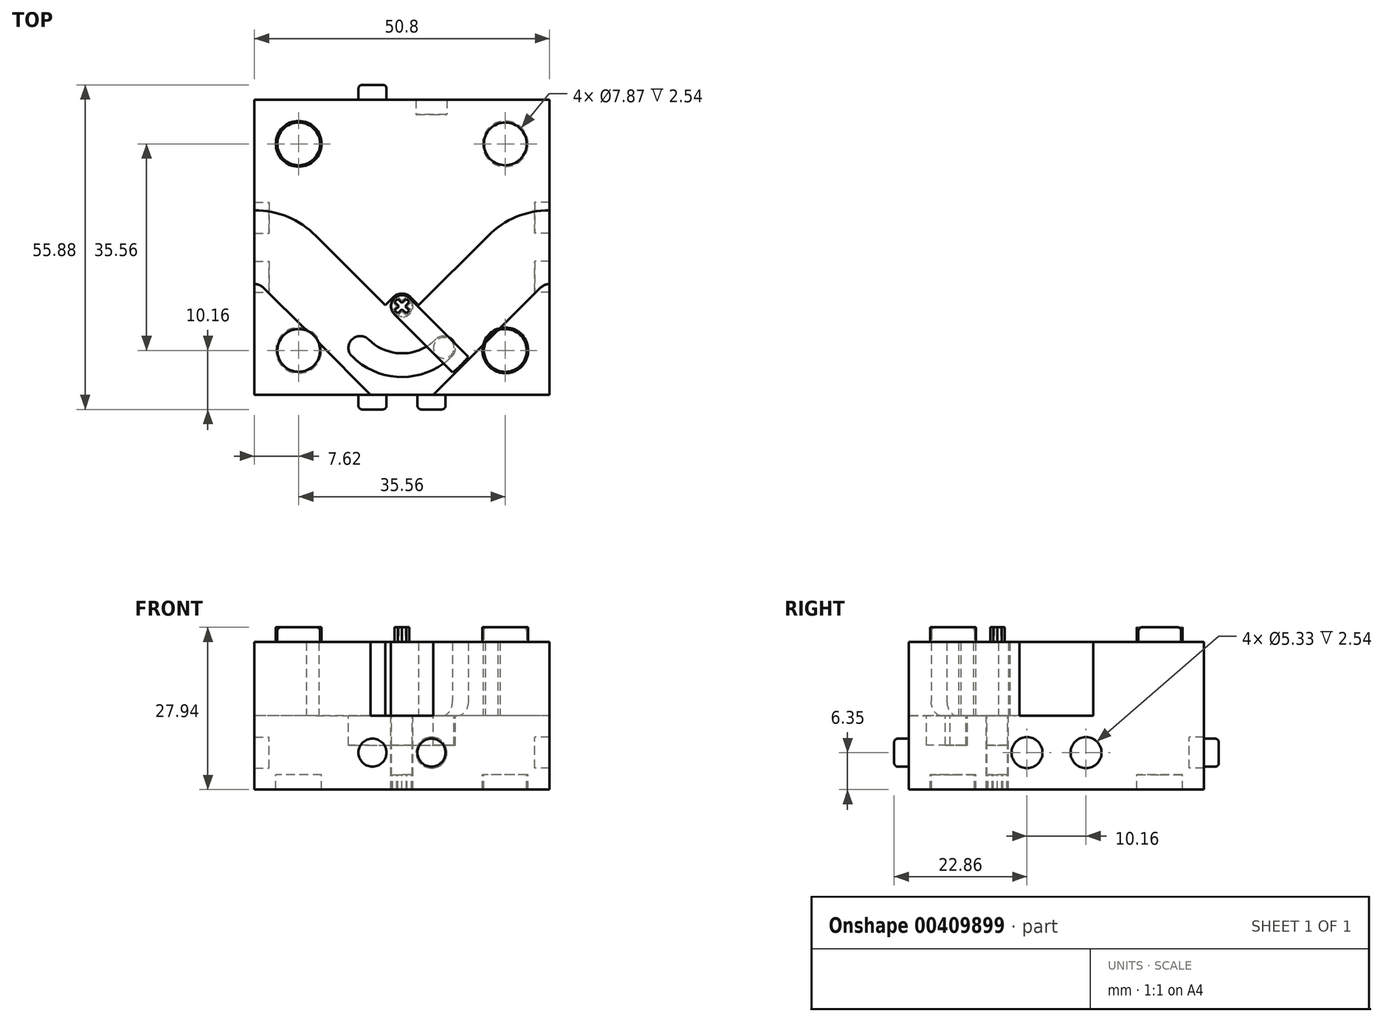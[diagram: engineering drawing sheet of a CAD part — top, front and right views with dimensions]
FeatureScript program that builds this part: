
annotation { "Feature Type Name" : "Feature", "Feature Type Description" : "" }
export const myFeature = defineFeature(function(context is Context, id is Id, definition is map)
    precondition{}
    {
        {
            var Q0;
            Q0=qCreatedBy(makeId("Top.planeOp"),FACE);
            var sketch = newSketch(context, id + "F0", { "sketchPlane" : qUnion([Q0])});
            skLineSegment(sketch, "E0.bottom", {"start": v(25.4, 25.4) * mm, "end": v(-25.4, 25.4) * mm});
            skLineSegment(sketch, "E0.top", {"start": v(25.4, -25.4) * mm, "end": v(-25.4, -25.4) * mm});
            skLineSegment(sketch, "E0.left", {"start": v(25.4, 25.4) * mm, "end": v(25.4, -25.4) * mm});
            skLineSegment(sketch, "E0.right", {"start": v(-25.4, 25.4) * mm, "end": v(-25.4, -25.4) * mm});
            skPoint(sketch, "E0.middle", {"position": v(0, 0) * mm});
            skPoint(sketch, "E1", {"position": v(25.4, 0) * mm});
            skPoint(sketch, "E2", {"position": v(-25.4, 0) * mm});
            skLineSegment(sketch, "E3", {"start": v(-25.4, 0) * mm, "end": v(25.4, 0) * mm, "construction": true});
            skLineSegment(sketch, "E4", {"start": v(0, 25.4) * mm, "end": v(0, -25.4) * mm, "construction": true});
            skCircle(sketch, "E5", {"center": v(0, 0) * mm, "radius": 2.54 * mm, "construction": true});
            skPoint(sketch, "E6", {"position": v(0, 2.54) * mm});
            skPoint(sketch, "E7", {"position": v(0, 5.08) * mm});
            skCircle(sketch, "E8", {"center": v(0, 0) * mm, "radius": 2.41 * mm});
            skCircle(sketch, "E9", {"center": v(0, 0) * mm, "radius": 2.67 * mm});
            skPoint(sketch, "E10", {"position": v(6.35, -25.4) * mm});
            skPoint(sketch, "E11", {"position": v(-6.35, -25.4) * mm});
            skCircle(sketch, "E12", {"center": v(0, 0) * mm, "radius": 5.08 * mm});
            skLineSegment(sketch, "E13", {"start": v(-6.35, -25.4) * mm, "end": v(6.35, -25.4) * mm});
            skLineSegment(sketch, "E14", {"start": v(-0.13, -26.91) * mm, "end": v(0.13, -26.91) * mm, "construction": true});
            skLineSegment(sketch, "E15", {"start": v(1.24, -2.36) * mm, "end": v(1.12, -2.14) * mm, "construction": true});
            skPoint(sketch, "E16", {"position": v(1.18, -2.25) * mm});
            skSolve(sketch);
        }
        {
            var Q0;
            Q0=qCreatedBy(makeId("Top.planeOp"),FACE);
            var sketch = newSketch(context, id + "F1", { "sketchPlane" : qUnion([Q0])});
            skLineSegment(sketch, "E17.0", {"start": v(1.35, -8.81) * mm, "end": v(11.4, -18.87) * mm});
            skLineSegment(sketch, "E18.0", {"start": v(8.71, -21.56) * mm, "end": v(-1.35, -11.5) * mm});
            skLineSegment(sketch, "E19.0", {"start": v(25.4, -25.4) * mm, "end": v(-25.4, -25.4) * mm});
            skLineSegment(sketch, "E20.0", {"start": v(25.4, 25.4) * mm, "end": v(25.4, 6.35) * mm});
            skLineSegment(sketch, "E21.0", {"start": v(25.4, 25.4) * mm, "end": v(-25.4, 25.4) * mm});
            skLineSegment(sketch, "E22.0", {"start": v(-25.4, 25.4) * mm, "end": v(-25.4, 6.35) * mm});
            skLineSegment(sketch, "E23", {"start": v(6.35, -38.04) * mm, "end": v(-6.35, -38.04) * mm, "construction": true});
            skLineSegment(sketch, "E24", {"start": v(35.56, -6.35) * mm, "end": v(35.56, 6.35) * mm, "construction": true});
            skPoint(sketch, "E25", {"position": v(0, -38.04) * mm});
            skPoint(sketch, "E26", {"position": v(35.56, 0) * mm});
            skLineSegment(sketch, "E27", {"start": v(10.15, -20.3) * mm, "end": v(0, -10.16) * mm, "construction": true});
            skLineSegment(sketch, "E28", {"start": v(14.82, 1.97) * mm, "end": v(2.87, -9.98) * mm});
            skLineSegment(sketch, "E29", {"start": v(0, -25.4) * mm, "end": v(0, 25.4) * mm, "construction": true});
            skLineSegment(sketch, "E30.trimOffspring", {"start": v(-25.4, -6.35) * mm, "end": v(-25.4, -25.4) * mm});
            skLineSegment(sketch, "E31.trimOffspring", {"start": v(25.4, -6.35) * mm, "end": v(25.4, -25.4) * mm});
            skArc(sketch, "E32", {"start": v(1.35, -8.81) * mm, "mid": v(-1.35, -8.81) * mm, "end": v(-1.35, -11.5) * mm});
            skArc(sketch, "E33", {"start": v(1.53, -8.63) * mm, "mid": v(0, -8) * mm, "end": v(-1.53, -8.63) * mm});
            skArc(sketch, "E34", {"start": v(25.4, 6.35) * mm, "mid": v(19.68, 5.21) * mm, "end": v(14.82, 1.97) * mm});
            skArc(sketch, "E35.MirrorCS", {"start": v(-25.4, 6.35) * mm, "mid": v(-19.68, 5.21) * mm, "end": v(-14.82, 1.97) * mm});
            skLineSegment(sketch, "E36.MirrorCS", {"start": v(-14.82, 1.97) * mm, "end": v(-2.87, -9.98) * mm});
            skLineSegment(sketch, "E37", {"start": v(-1.35, -11.5) * mm, "end": v(-2.87, -9.98) * mm, "construction": true});
            skLineSegment(sketch, "E38", {"start": v(-2.87, -9.98) * mm, "end": v(-2.87, -9.98) * mm});
            skLineSegment(sketch, "E39", {"start": v(-1.53, -8.63) * mm, "end": v(-2.87, -9.98) * mm});
            skLineSegment(sketch, "E40", {"start": v(1.53, -8.63) * mm, "end": v(2.87, -9.98) * mm});
            skLineSegment(sketch, "E41", {"start": v(-1.35, -11.5) * mm, "end": v(1.53, -8.63) * mm, "construction": true});
            skArc(sketch, "E42", {"start": v(-25.4, -6.35) * mm, "mid": v(-24.54, -6.52) * mm, "end": v(-23.8, -7.01) * mm});
            skLineSegment(sketch, "E43", {"start": v(-14.82, 1.97) * mm, "end": v(-25.4, -8.6) * mm, "construction": true});
            skLineSegment(sketch, "E44", {"start": v(-23.8, -7.01) * mm, "end": v(-11.85, -18.96) * mm});
            skLineSegment(sketch, "E45", {"start": v(-5.41, -25.4) * mm, "end": v(-10.33, -20.49) * mm});
            skLineSegment(sketch, "E46", {"start": v(-10.33, -20.49) * mm, "end": v(-10.33, -20.49) * mm});
            skLineSegment(sketch, "E47", {"start": v(-1.35, -11.5) * mm, "end": v(0, -10.16) * mm, "construction": true});
            skLineSegment(sketch, "E48", {"start": v(-10.33, -20.49) * mm, "end": v(-11.85, -18.96) * mm});
            skLineSegment(sketch, "E49.MirrorCS", {"start": v(5.41, -25.4) * mm, "end": v(10.33, -20.49) * mm});
            skLineSegment(sketch, "E50.MirrorCS", {"start": v(10.33, -20.49) * mm, "end": v(10.33, -20.49) * mm});
            skLineSegment(sketch, "E51.MirrorCS", {"start": v(10.33, -20.49) * mm, "end": v(11.85, -18.96) * mm});
            skLineSegment(sketch, "E52.MirrorCS", {"start": v(23.8, -7.01) * mm, "end": v(11.85, -18.96) * mm});
            skArc(sketch, "E53", {"start": v(25.4, -6.35) * mm, "mid": v(24.54, -6.52) * mm, "end": v(23.8, -7.01) * mm});
            skPoint(sketch, "E54", {"position": v(0, 0) * mm});
            skLineSegment(sketch, "E55", {"start": v(-0.98, -8.53) * mm, "end": v(-1.11, -8.31) * mm, "construction": true});
            skLineSegment(sketch, "E56", {"start": v(10.33, -20.49) * mm, "end": v(10.15, -20.3) * mm, "construction": true});
            skCircle(sketch, "E57", {"center": v(0, -10.16) * mm, "radius": 14.35 * mm});
            skSolve(sketch);
        }
        {
            var Q0;
            Q0=qCreatedBy(makeId("Top.planeOp"),FACE);
            var sketch = newSketch(context, id + "F2", { "sketchPlane" : qUnion([Q0])});
            skLineSegment(sketch, "E58.0", {"start": v(-25.4, 25.4) * mm, "end": v(-25.4, -25.4) * mm, "construction": true});
            skLineSegment(sketch, "E58.1", {"start": v(0, 25.4) * mm, "end": v(0, -25.4) * mm, "construction": true});
            skLineSegment(sketch, "E58.2", {"start": v(-25.4, 0) * mm, "end": v(25.4, 0) * mm, "construction": true});
            skLineSegment(sketch, "E58.3", {"start": v(25.4, 25.4) * mm, "end": v(-25.4, 25.4) * mm, "construction": true});
            skLineSegment(sketch, "E58.4", {"start": v(25.4, -25.4) * mm, "end": v(-25.4, -25.4) * mm, "construction": true});
            skLineSegment(sketch, "E58.5", {"start": v(25.4, 25.4) * mm, "end": v(25.4, -25.4) * mm, "construction": true});
            skCircle(sketch, "E59", {"center": v(17.78, 17.78) * mm, "radius": 3.81 * mm, "construction": true});
            skLineSegment(sketch, "E60", {"start": v(17.78, 17.78) * mm, "end": v(17.78, 25.4) * mm, "construction": true});
            skLineSegment(sketch, "E61", {"start": v(17.78, 17.78) * mm, "end": v(25.4, 17.78) * mm, "construction": true});
            skLineSegment(sketch, "E62", {"start": v(19.27, 14.41) * mm, "end": v(19.38, 14.18) * mm, "construction": true});
            skCircle(sketch, "E63", {"center": v(17.78, 17.78) * mm, "radius": 3.68 * mm});
            skCircle(sketch, "E64", {"center": v(17.78, 17.78) * mm, "radius": 3.94 * mm});
            skCircle(sketch, "E65.MirrorC", {"center": v(17.78, -17.78) * mm, "radius": 3.94 * mm});
            skCircle(sketch, "E66.MirrorC", {"center": v(17.78, -17.78) * mm, "radius": 3.68 * mm});
            skCircle(sketch, "E67.MirrorC", {"center": v(-17.78, -17.78) * mm, "radius": 3.68 * mm});
            skCircle(sketch, "E68.MirrorC", {"center": v(-17.78, -17.78) * mm, "radius": 3.94 * mm});
            skCircle(sketch, "E69.MirrorC", {"center": v(-17.78, 17.78) * mm, "radius": 3.68 * mm});
            skCircle(sketch, "E70.MirrorC", {"center": v(-17.78, 17.78) * mm, "radius": 3.94 * mm});
            skPoint(sketch, "E71.positionSnap0", {"position": v(19.33, 14.3) * mm});
            skLineSegment(sketch, "E72.0", {"start": v(1.17, -9) * mm, "end": v(-1.17, -11.33) * mm, "construction": true});
            skLineSegment(sketch, "E73.0", {"start": v(1.17, -11.33) * mm, "end": v(-1.17, -9) * mm, "construction": true});
            skLineSegment(sketch, "E74", {"start": v(1.08, -11.24) * mm, "end": v(0.72, -11.6) * mm, "construction": true});
            skLineSegment(sketch, "E75", {"start": v(0.72, -11.6) * mm, "end": v(0, -10.88) * mm, "construction": true});
            skLineSegment(sketch, "E76", {"start": v(0, -10.16) * mm, "end": v(0, -11.06) * mm, "construction": true});
            skLineSegment(sketch, "E77", {"start": v(0.99, -11.15) * mm, "end": v(0.72, -11.42) * mm});
            skLineSegment(sketch, "E78", {"start": v(0.72, -11.42) * mm, "end": v(0, -10.7) * mm});
            skLineSegment(sketch, "E79", {"start": v(1.17, -11.33) * mm, "end": v(0.72, -11.78) * mm});
            skLineSegment(sketch, "E80", {"start": v(0.72, -11.78) * mm, "end": v(0, -11.06) * mm});
            skLineSegment(sketch, "E81", {"start": v(0.96, -11.18) * mm, "end": v(1.14, -11.36) * mm, "construction": true});
            skLineSegment(sketch, "E82", {"start": v(0.63, -11.33) * mm, "end": v(0.45, -11.5) * mm, "construction": true});
            skLineSegment(sketch, "E83.MirrorCS", {"start": v(1.62, -10.88) * mm, "end": v(0.9, -10.16) * mm});
            skLineSegment(sketch, "E84.MirrorCS", {"start": v(0.99, -11.15) * mm, "end": v(1.26, -10.88) * mm});
            skLineSegment(sketch, "E85.MirrorCS", {"start": v(1.17, -11.33) * mm, "end": v(1.62, -10.88) * mm});
            skLineSegment(sketch, "E86.MirrorCS", {"start": v(1.26, -10.88) * mm, "end": v(0.54, -10.16) * mm});
            skLineSegment(sketch, "E87.MirrorCS", {"start": v(-0.99, -11.15) * mm, "end": v(-0.72, -11.42) * mm});
            skLineSegment(sketch, "E88.MirrorCS", {"start": v(-1.62, -10.88) * mm, "end": v(-0.9, -10.16) * mm});
            skLineSegment(sketch, "E89.MirrorCS", {"start": v(-0.72, -11.42) * mm, "end": v(0, -10.7) * mm});
            skLineSegment(sketch, "E90.MirrorCS", {"start": v(-0.99, -11.15) * mm, "end": v(-1.26, -10.88) * mm});
            skLineSegment(sketch, "E91.MirrorCS", {"start": v(-1.17, -11.33) * mm, "end": v(-0.72, -11.78) * mm});
            skLineSegment(sketch, "E92.MirrorCS", {"start": v(-1.17, -11.33) * mm, "end": v(-1.62, -10.88) * mm});
            skLineSegment(sketch, "E93.MirrorCS", {"start": v(-1.26, -10.88) * mm, "end": v(-0.54, -10.16) * mm});
            skLineSegment(sketch, "E94.MirrorCS", {"start": v(-0.72, -11.78) * mm, "end": v(0, -11.06) * mm});
            skLineSegment(sketch, "E95", {"start": v(0, -10.16) * mm, "end": v(0.9, -10.16) * mm, "construction": true});
            skLineSegment(sketch, "E96.MirrorCS", {"start": v(1.62, -9.44) * mm, "end": v(0.9, -10.16) * mm});
            skLineSegment(sketch, "E97.MirrorCS", {"start": v(1.26, -9.44) * mm, "end": v(0.54, -10.16) * mm});
            skLineSegment(sketch, "E98.MirrorCS", {"start": v(1.17, -9) * mm, "end": v(1.62, -9.44) * mm});
            skLineSegment(sketch, "E99.MirrorCS", {"start": v(0.99, -9.17) * mm, "end": v(1.26, -9.44) * mm});
            skLineSegment(sketch, "E100.MirrorCS", {"start": v(0.99, -9.17) * mm, "end": v(0.72, -8.9) * mm});
            skLineSegment(sketch, "E101.MirrorCS", {"start": v(1.17, -9) * mm, "end": v(0.72, -8.54) * mm});
            skLineSegment(sketch, "E102.MirrorCS", {"start": v(0.72, -8.9) * mm, "end": v(0, -9.62) * mm});
            skLineSegment(sketch, "E103.MirrorCS", {"start": v(0.72, -8.54) * mm, "end": v(0, -9.26) * mm});
            skLineSegment(sketch, "E104.MirrorCS", {"start": v(-0.72, -8.9) * mm, "end": v(0, -9.62) * mm});
            skLineSegment(sketch, "E105.MirrorCS", {"start": v(-0.72, -8.54) * mm, "end": v(0, -9.26) * mm});
            skLineSegment(sketch, "E106.MirrorCS", {"start": v(-0.99, -9.17) * mm, "end": v(-0.72, -8.9) * mm});
            skLineSegment(sketch, "E107.MirrorCS", {"start": v(-1.17, -9) * mm, "end": v(-0.72, -8.54) * mm});
            skLineSegment(sketch, "E108.MirrorCS", {"start": v(-0.99, -9.17) * mm, "end": v(-1.26, -9.44) * mm});
            skLineSegment(sketch, "E109.MirrorCS", {"start": v(-1.26, -9.44) * mm, "end": v(-0.54, -10.16) * mm});
            skLineSegment(sketch, "E110.MirrorCS", {"start": v(-1.62, -9.44) * mm, "end": v(-0.9, -10.16) * mm});
            skLineSegment(sketch, "E111.MirrorCS", {"start": v(-1.17, -9) * mm, "end": v(-1.62, -9.44) * mm});
            skPoint(sketch, "E112.0", {"position": v(0, -10.16) * mm});
            skSolve(sketch);
        }
        {
            var Q0;
            Q0=qCreatedBy(makeId("Top.planeOp"),FACE);
            var sketch = newSketch(context, id + "F3", { "sketchPlane" : qUnion([Q0])});
            skLineSegment(sketch, "E113.0", {"start": v(25.4, -25.4) * mm, "end": v(-25.4, -25.4) * mm});
            skLineSegment(sketch, "E114.0", {"start": v(25.4, 25.4) * mm, "end": v(25.4, -25.4) * mm});
            skLineSegment(sketch, "E115.0", {"start": v(25.4, 25.4) * mm, "end": v(-25.4, 25.4) * mm});
            skLineSegment(sketch, "E116.0", {"start": v(-25.4, 25.4) * mm, "end": v(-25.4, -25.4) * mm});
            skPoint(sketch, "E117.0", {"position": v(0, -10.16) * mm});
            skLineSegment(sketch, "E118.0", {"start": v(8.98, -19.14) * mm, "end": v(0, -10.16) * mm, "construction": true});
            skCircle(sketch, "E119", {"center": v(7.18, -17.34) * mm, "radius": 1.9 * mm, "construction": true});
            skLineSegment(sketch, "E120", {"start": v(8.51, -18.53) * mm, "end": v(8.7, -18.7) * mm, "construction": true});
            skPoint(sketch, "E121", {"position": v(8.6, -18.61) * mm});
            skArc(sketch, "E122", {"start": v(8.62, -18.78) * mm, "mid": v(8.62, -15.9) * mm, "end": v(5.75, -15.9) * mm});
            skCircle(sketch, "E123", {"center": v(7.18, -17.34) * mm, "radius": 1.78 * mm});
            skLineSegment(sketch, "E124", {"start": v(0, -25.4) * mm, "end": v(0, -10.16) * mm, "construction": true});
            skArc(sketch, "E125.MirrorCS", {"start": v(-8.62, -18.78) * mm, "mid": v(-8.62, -15.9) * mm, "end": v(-5.75, -15.9) * mm});
            skArc(sketch, "E126", {"start": v(8.62, -18.78) * mm, "mid": v(0, -22.35) * mm, "end": v(-8.62, -18.78) * mm});
            skArc(sketch, "E127", {"start": v(5.75, -15.9) * mm, "mid": v(0, -18.29) * mm, "end": v(-5.75, -15.9) * mm});
            skLineSegment(sketch, "E128", {"start": v(7.18, -17.34) * mm, "end": v(7.37, -19.11) * mm, "construction": true});
            skLineSegment(sketch, "E129", {"start": v(7.18, -17.34) * mm, "end": v(6.12, -15.76) * mm, "construction": true});
            skCircle(sketch, "E130", {"center": v(0, -10.16) * mm, "radius": 1.78 * mm});
            skCircle(sketch, "E131", {"center": v(0, -10.16) * mm, "radius": 1.9 * mm});
            skLineSegment(sketch, "E132", {"start": v(0, -10.16) * mm, "end": v(0.96, -11.65) * mm, "construction": true});
            skLineSegment(sketch, "E133", {"start": v(0, -10.16) * mm, "end": v(1.04, -11.76) * mm, "construction": true});
            skSolve(sketch);
        }
        {
            var Q0;
            Q0=qCreatedBy(makeId("Top.planeOp"),FACE);
            var sketch = newSketch(context, id + "F4", { "sketchPlane" : qUnion([Q0])});
            skCircle(sketch, "E134.0", {"center": v(0, -10.16) * mm, "radius": 1.78 * mm});
            skCircle(sketch, "E134.1", {"center": v(0, -10.16) * mm, "radius": 1.9 * mm});
            skLineSegment(sketch, "E135.0", {"start": v(25.4, 25.4) * mm, "end": v(25.4, -25.4) * mm});
            skLineSegment(sketch, "E136.0", {"start": v(25.4, 25.4) * mm, "end": v(-25.4, 25.4) * mm});
            skLineSegment(sketch, "E137.0", {"start": v(-25.4, 25.4) * mm, "end": v(-25.4, -25.4) * mm});
            skLineSegment(sketch, "E138.0", {"start": v(25.4, -25.4) * mm, "end": v(-25.4, -25.4) * mm});
            skSolve(sketch);
        }
        {
            var Q0;
            {var subQ0=sQuery(id+"F1.wireOp",EDGE,"E31.trimOffspring");Q0=makeQuery(id+"F1.imprint","IMPRINT",FACE,{"disambiguationData":[TD([[makeQuery(id+"F1.imprint","IMPRINT",EDGE,{"derivedFrom":subQ0}),-1.0]])]});}
            var Q1;
            Q1=makeQuery(id+"F1.imprint","IMPRINT",FACE,{"disambiguationData":[TD([[makeQuery(id+"F1.imprint","IMPRINT",EDGE,{"derivedFrom":sQuery(id+"F1.wireOp",EDGE,"E20.0")}),-1.0]])]});
            var Q2;
            {var subQ0=sQuery(id+"F1.wireOp",EDGE,"E30.trimOffspring");Q2=makeQuery(id+"F1.imprint","IMPRINT",FACE,{"disambiguationData":[TD([[makeQuery(id+"F1.imprint","IMPRINT",EDGE,{"derivedFrom":subQ0}),1.0]])]});}
            var Q3;
            Q3=makeQuery(id+"F1.imprint","IMPRINT",FACE,{"disambiguationData":[TD([[makeQuery(id+"F1.imprint","IMPRINT",EDGE,{"derivedFrom":sQuery(id+"F1.wireOp",EDGE,"E33")}),-1.0]])]});
            var Q4;
            {var subQ0=sQuery(id+"F1.wireOp",EDGE,"E17.0");Q4=makeQuery(id+"F1.imprint","IMPRINT",FACE,{"disambiguationData":[TD([[makeQuery(id+"F1.imprint","IMPRINT",EDGE,{"derivedFrom":subQ0}),-1.0]])]});}
            var Q5;
            {var subQ0=sQuery(id+"F1.wireOp",EDGE,"E28");Q5=makeQuery(id+"F1.imprint","IMPRINT",FACE,{"disambiguationData":[TD([[makeQuery(id+"F1.imprint","IMPRINT",EDGE,{"derivedFrom":subQ0}),-1.0]])]});}
            extrude(context, id + "F5", {"entities" : qUnion([Q0, Q1, Q2, Q3, Q4, Q5]), "depth" : 12.7 * mm});
        }
        {
            var Q0;
            Q0=makeQuery(id+"F2.imprint","IMPRINT",FACE,{"disambiguationData":[TD([[makeQuery(id+"F2.imprint","IMPRINT",EDGE,{"derivedFrom":sQuery(id+"F2.wireOp",EDGE,"E66.MirrorC")}),-1.0]])]});
            var Q1;
            Q1=makeQuery(id+"F2.imprint","IMPRINT",FACE,{"disambiguationData":[TD([[makeQuery(id+"F2.imprint","IMPRINT",EDGE,{"derivedFrom":sQuery(id+"F2.wireOp",EDGE,"E63")}),1.0]])]});
            var Q2;
            Q2=makeQuery(id+"F2.imprint","IMPRINT",FACE,{"disambiguationData":[TD([[makeQuery(id+"F2.imprint","IMPRINT",EDGE,{"derivedFrom":sQuery(id+"F2.wireOp",EDGE,"E69.MirrorC")}),-1.0]])]});
            var Q3;
            Q3=makeQuery(id+"F2.imprint","IMPRINT",FACE,{"disambiguationData":[TD([[makeQuery(id+"F2.imprint","IMPRINT",EDGE,{"derivedFrom":sQuery(id+"F2.wireOp",EDGE,"E67.MirrorC")}),1.0]])]});
            var Q4;
            {var subQ1=sQuery(id+"F2.wireOp",EDGE,"E77");Q4=makeQuery(id+"F2.imprint","IMPRINT",FACE,{"disambiguationData":[TD([[makeQuery(id+"F2.imprint","IMPRINT",EDGE,{"derivedFrom":subQ1}),-1.0]])]});}
            extrude(context, id + "F6", {"entities" : qUnion([Q0, Q1, Q2, Q3, Q4]), "operationType" : NewBodyOperationType.ADD, "depth" : 15.24 * mm});
        }
        {
            var Q0;
            Q0=makeQuery(id+"F3.imprint","IMPRINT",FACE,{"disambiguationData":[TD([[makeQuery(id+"F3.imprint","IMPRINT",EDGE,{"derivedFrom":sQuery(id+"F3.wireOp",EDGE,"E113.0")}),-1.0]])]});
            var Q1;
            Q1=makeQuery(id+"F3.imprint","IMPRINT",FACE,{"disambiguationData":[TD([[makeQuery(id+"F3.imprint","IMPRINT",EDGE,{"derivedFrom":sQuery(id+"F3.wireOp",EDGE,"E123")}),1.0]])]});
            var Q2;
            Q2=makeQuery(id+"F3.imprint","IMPRINT",FACE,{"disambiguationData":[TD([[makeQuery(id+"F3.imprint","IMPRINT",EDGE,{"derivedFrom":sQuery(id+"F3.wireOp",EDGE,"E130")}),1.0]])]});
            extrude(context, id + "F7", {"entities" : qUnion([Q0, Q1, Q2]), "oppositeDirection" : true, "depth" : 5.08 * mm});
        }
        {
            var Q0;
            Q0=makeQuery(id+"F4.imprint","IMPRINT",FACE,{"disambiguationData":[TD([[makeQuery(id+"F4.imprint","IMPRINT",EDGE,{"derivedFrom":sQuery(id+"F4.wireOp",EDGE,"E134.1")}),-1.0]])]});
            var Q1;
            Q1=makeQuery(id+"F4.imprint","IMPRINT",FACE,{"disambiguationData":[TD([[makeQuery(id+"F4.imprint","IMPRINT",EDGE,{"derivedFrom":sQuery(id+"F4.wireOp",EDGE,"E134.0")}),1.0]])]});
            extrude(context, id + "F8", {"entities" : qUnion([Q0, Q1]), "oppositeDirection" : true, "depth" : 12.7 * mm, "hasSecondDirection" : true, "secondDirectionOppositeDirection" : true, "secondDirectionDepth" : 5.08 * mm});
        }
        {
            var Q0;
            Q0=makeQuery(id+"F2.imprint","IMPRINT",FACE,{"disambiguationData":[TD([[makeQuery(id+"F2.imprint","IMPRINT",EDGE,{"derivedFrom":sQuery(id+"F2.wireOp",EDGE,"E67.MirrorC")}),1.0]])]});
            var Q1;
            Q1=makeQuery(id+"F2.imprint","IMPRINT",FACE,{"disambiguationData":[TD([[makeQuery(id+"F2.imprint","IMPRINT",EDGE,{"derivedFrom":sQuery(id+"F2.wireOp",EDGE,"E67.MirrorC")}),-1.0]])]});
            var Q2;
            Q2=makeQuery(id+"F2.imprint","IMPRINT",FACE,{"disambiguationData":[TD([[makeQuery(id+"F2.imprint","IMPRINT",EDGE,{"derivedFrom":sQuery(id+"F2.wireOp",EDGE,"E69.MirrorC")}),-1.0]])]});
            var Q3;
            Q3=makeQuery(id+"F2.imprint","IMPRINT",FACE,{"disambiguationData":[TD([[makeQuery(id+"F2.imprint","IMPRINT",EDGE,{"derivedFrom":sQuery(id+"F2.wireOp",EDGE,"E69.MirrorC")}),1.0]])]});
            var Q4;
            Q4=makeQuery(id+"F2.imprint","IMPRINT",FACE,{"disambiguationData":[TD([[makeQuery(id+"F2.imprint","IMPRINT",EDGE,{"derivedFrom":sQuery(id+"F2.wireOp",EDGE,"E63")}),1.0]])]});
            var Q5;
            Q5=makeQuery(id+"F2.imprint","IMPRINT",FACE,{"disambiguationData":[TD([[makeQuery(id+"F2.imprint","IMPRINT",EDGE,{"derivedFrom":sQuery(id+"F2.wireOp",EDGE,"E63")}),-1.0]])]});
            var Q6;
            Q6=makeQuery(id+"F2.imprint","IMPRINT",FACE,{"disambiguationData":[TD([[makeQuery(id+"F2.imprint","IMPRINT",EDGE,{"derivedFrom":sQuery(id+"F2.wireOp",EDGE,"E66.MirrorC")}),-1.0]])]});
            var Q7;
            Q7=makeQuery(id+"F2.imprint","IMPRINT",FACE,{"disambiguationData":[TD([[makeQuery(id+"F2.imprint","IMPRINT",EDGE,{"derivedFrom":sQuery(id+"F2.wireOp",EDGE,"E65.MirrorC")}),-1.0]])]});
            var Q8;
            {var subQ3=sQuery(id+"F2.wireOp",EDGE,"E78");Q8=makeQuery(id+"F2.imprint","IMPRINT",FACE,{"disambiguationData":[TD([[makeQuery(id+"F2.imprint","IMPRINT",EDGE,{"derivedFrom":subQ3}),-1.0]])]});}
            var Q9;
            {var subQ6=sQuery(id+"F2.wireOp",EDGE,"E78");Q9=makeQuery(id+"F2.imprint","IMPRINT",FACE,{"disambiguationData":[TD([[makeQuery(id+"F2.imprint","IMPRINT",EDGE,{"derivedFrom":subQ6}),1.0]])]});}
            var Q10;
            {var subQ3=sQuery(id+"F2.wireOp",EDGE,"E81");Q10=makeQuery(id+"F2.imprint","IMPRINT",FACE,{"disambiguationData":[TD([[makeQuery(id+"F2.imprint","IMPRINT",EDGE,{"derivedFrom":subQ3}),1.0]])]});}
            extrude(context, id + "F9", {"entities" : qUnion([Q0, Q1, Q2, Q3, Q4, Q5, Q6, Q7, Q8, Q9, Q10]), "operationType" : NewBodyOperationType.REMOVE, "oppositeDirection" : true, "depth" : 12.7 * mm, "hasSecondDirection" : true, "secondDirectionOppositeDirection" : true, "secondDirectionDepth" : 10.16 * mm});
        }
        {
            var Q0;
            Q0=makeQuery(id+"F5.opExtrude","SWEPT_BODY",BODY,{"disambiguationData":[OSD([sQuery(id+"F1.wireOp",EDGE,"07ce15e0-389a-4b33-b96a-b9eb0d6417ea.0"),sQuery(id+"F1.wireOp",EDGE,"2ea3173f-9e5d-47db-bc64-ed2cd4916a22.0"),sQuery(id+"F1.wireOp",EDGE,"1fc487c8-3388-41be-b45a-3c84602bca13.0"),sQuery(id+"F1.wireOp",EDGE,"E19.0"),sQuery(id+"F1.wireOp",EDGE,"E31.trimOffspring")])]});
            var Q1;
            Q1=makeQuery(id+"F7.opExtrude","SWEPT_BODY",BODY,{"disambiguationData":[OSD([sQuery(id+"F3.wireOp",EDGE,"E113.0"),sQuery(id+"F3.wireOp",EDGE,"E114.0"),sQuery(id+"F3.wireOp",EDGE,"E115.0"),sQuery(id+"F3.wireOp",EDGE,"E116.0"),sQuery(id+"F3.wireOp",EDGE,"E122"),sQuery(id+"F3.wireOp",EDGE,"E125.MirrorCS"),sQuery(id+"F3.wireOp",EDGE,"E126"),sQuery(id+"F3.wireOp",EDGE,"E127"),sQuery(id+"F3.wireOp",EDGE,"E131")])]});
            var Q2;
            Q2=makeQuery(id+"F5.opExtrude","SWEPT_BODY",BODY,{"disambiguationData":[OSD([sQuery(id+"F1.wireOp",EDGE,"90c61b00-249b-4847-8f0a-689f453f4bd6.0"),sQuery(id+"F1.wireOp",EDGE,"aaa51523-57ab-4ff3-b2ff-3d760ec803aa.0"),sQuery(id+"F1.wireOp",EDGE,"1fc487c8-3388-41be-b45a-3c84602bca13.0"),sQuery(id+"F1.wireOp",EDGE,"E19.0"),sQuery(id+"F1.wireOp",EDGE,"E30.trimOffspring")])]});
            var Q3;
            Q3=makeQuery(id+"F8.opExtrude","SWEPT_BODY",BODY,{"disambiguationData":[OSD([sQuery(id+"F4.wireOp",EDGE,"E134.1"),sQuery(id+"F4.wireOp",EDGE,"E135.0"),sQuery(id+"F4.wireOp",EDGE,"E136.0"),sQuery(id+"F4.wireOp",EDGE,"E137.0"),sQuery(id+"F4.wireOp",EDGE,"E138.0")])]});
            var Q4;
            Q4=makeQuery(id+"F5.opExtrude","SWEPT_BODY",BODY,{"disambiguationData":[OSD([sQuery(id+"F1.wireOp",EDGE,"d973afc5-03ed-41d9-9e6c-79cc070b5d1a.0"),sQuery(id+"F1.wireOp",EDGE,"1fc487c8-3388-41be-b45a-3c84602bca13.0"),sQuery(id+"F1.wireOp",EDGE,"E20.0"),sQuery(id+"F1.wireOp",EDGE,"E21.0"),sQuery(id+"F1.wireOp",EDGE,"E22.0"),sQuery(id+"F1.wireOp",EDGE,"b72e6335-8749-4926-bdcc-0623d4d98a26")])]});
            booleanBodies(context, id + "F10", {"operationType" : BooleanOperationType.UNION, "tools" : qUnion([Q0, Q1, Q2, Q3, Q4])});
        }
        {
            var Q0;
            Q0=qCreatedBy(makeId("Right.planeOp"),FACE);
            var sketch = newSketch(context, id + "F11", { "sketchPlane" : qUnion([Q0])});
            skPoint(sketch, "E139", {"position": v(-5.08, -6.35) * mm});
            skPoint(sketch, "E140", {"position": v(-2.67, -6.35) * mm});
            skPoint(sketch, "E141", {"position": v(-2.41, -6.35) * mm});
            skPoint(sketch, "E142", {"position": v(2.41, -6.35) * mm});
            skPoint(sketch, "E143", {"position": v(2.67, -6.35) * mm});
            skPoint(sketch, "E144", {"position": v(5.08, -6.35) * mm});
            skCircle(sketch, "E145", {"center": v(-5.08, -6.35) * mm, "radius": 2.41 * mm});
            skCircle(sketch, "E146", {"center": v(-5.08, -6.35) * mm, "radius": 2.67 * mm});
            skCircle(sketch, "E147", {"center": v(5.08, -6.35) * mm, "radius": 2.41 * mm});
            skCircle(sketch, "E148", {"center": v(5.08, -6.35) * mm, "radius": 2.67 * mm});
            skLineSegment(sketch, "E149", {"start": v(-2.67, 0) * mm, "end": v(-5.08, 0) * mm});
            skLineSegment(sketch, "E150", {"start": v(5.08, 0) * mm, "end": v(2.67, 0) * mm});
            skLineSegment(sketch, "E151", {"start": v(-2.41, 0) * mm, "end": v(-2.67, 0) * mm});
            skLineSegment(sketch, "E152", {"start": v(2.67, 0) * mm, "end": v(2.41, 0) * mm});
            skLineSegment(sketch, "E153", {"start": v(-25.4, 0) * mm, "end": v(-25.4, -12.7) * mm});
            skLineSegment(sketch, "E154", {"start": v(25.4, -12.7) * mm, "end": v(25.4, 12.7) * mm});
            skPoint(sketch, "E155", {"position": v(-25.4, -6.35) * mm});
            skPoint(sketch, "E156", {"position": v(25.4, 0) * mm});
            skPoint(sketch, "E157", {"position": v(25.4, -6.35) * mm});
            skSolve(sketch);
        }
        {
            var Q0;
            Q0=qCreatedBy(makeId("Front.planeOp"),FACE);
            var sketch = newSketch(context, id + "F12", { "sketchPlane" : qUnion([Q0])});
            skPoint(sketch, "E158", {"position": v(-154.37, 0) * mm});
            skPoint(sketch, "E159", {"position": v(-154.37, -6.35) * mm});
            skPoint(sketch, "E160", {"position": v(5.08, -6.35) * mm});
            skPoint(sketch, "E161", {"position": v(2.67, -6.35) * mm});
            skPoint(sketch, "E162", {"position": v(2.41, -6.35) * mm});
            skPoint(sketch, "E163", {"position": v(-2.41, -6.35) * mm});
            skPoint(sketch, "E164", {"position": v(-2.67, -6.35) * mm});
            skPoint(sketch, "E165", {"position": v(-5.08, -6.35) * mm});
            skCircle(sketch, "E166", {"center": v(5.08, -6.35) * mm, "radius": 2.41 * mm});
            skCircle(sketch, "E167", {"center": v(5.08, -6.35) * mm, "radius": 2.67 * mm});
            skCircle(sketch, "E168", {"center": v(-5.08, -6.35) * mm, "radius": 2.67 * mm});
            skCircle(sketch, "E169", {"center": v(-5.08, -6.35) * mm, "radius": 2.41 * mm});
            skLineSegment(sketch, "E170", {"start": v(-2.67, 0) * mm, "end": v(-5.08, 0) * mm});
            skLineSegment(sketch, "E171", {"start": v(5.08, 0) * mm, "end": v(2.67, 0) * mm});
            skLineSegment(sketch, "E172", {"start": v(-2.41, 0) * mm, "end": v(-2.67, 0) * mm});
            skLineSegment(sketch, "E173", {"start": v(2.67, 0) * mm, "end": v(2.41, 0) * mm});
            skLineSegment(sketch, "E174", {"start": v(-25.4, 0) * mm, "end": v(-25.4, -12.7) * mm});
            skLineSegment(sketch, "E175", {"start": v(25.4, -12.7) * mm, "end": v(25.4, 0) * mm});
            skPoint(sketch, "E176", {"position": v(-25.4, -6.35) * mm});
            skPoint(sketch, "E177", {"position": v(25.4, -6.35) * mm});
            skSolve(sketch);
        }
        {
            var Q0;
            Q0=makeQuery(id+"F12.imprint","IMPRINT",FACE,{"disambiguationData":[TD([[makeQuery(id+"F12.imprint","IMPRINT",EDGE,{"derivedFrom":sQuery(id+"F12.wireOp",EDGE,"E169")}),1.0]])]});
            extrude(context, id + "F13", {"entities" : qUnion([Q0]), "operationType" : NewBodyOperationType.ADD, "oppositeDirection" : true, "depth" : 27.94 * mm, "hasSecondDirection" : true, "secondDirectionOppositeDirection" : true, "secondDirectionDepth" : 22.86 * mm});
        }
        {
            var Q0;
            Q0=makeQuery(id+"F12.imprint","IMPRINT",FACE,{"disambiguationData":[TD([[makeQuery(id+"F12.imprint","IMPRINT",EDGE,{"derivedFrom":sQuery(id+"F12.wireOp",EDGE,"E169")}),1.0]])]});
            var Q1;
            Q1=makeQuery(id+"F12.imprint","IMPRINT",FACE,{"disambiguationData":[TD([[makeQuery(id+"F12.imprint","IMPRINT",EDGE,{"derivedFrom":sQuery(id+"F12.wireOp",EDGE,"E166")}),1.0]])]});
            extrude(context, id + "F14", {"entities" : qUnion([Q0, Q1]), "operationType" : NewBodyOperationType.ADD, "depth" : 27.94 * mm, "hasSecondDirection" : true, "secondDirectionOppositeDirection" : false, "secondDirectionDepth" : 22.86 * mm});
        }
        {
            var Q0;
            Q0=makeQuery(id+"F11.imprint","IMPRINT",FACE,{"disambiguationData":[TD([[makeQuery(id+"F11.imprint","IMPRINT",EDGE,{"derivedFrom":sQuery(id+"F11.wireOp",EDGE,"E145")}),1.0]])]});
            var Q1;
            Q1=makeQuery(id+"F11.imprint","IMPRINT",FACE,{"disambiguationData":[TD([[makeQuery(id+"F11.imprint","IMPRINT",EDGE,{"derivedFrom":sQuery(id+"F11.wireOp",EDGE,"E147")}),1.0]])]});
            var Q2;
            Q2=makeQuery(id+"F11.imprint","IMPRINT",FACE,{"disambiguationData":[TD([[makeQuery(id+"F11.imprint","IMPRINT",EDGE,{"derivedFrom":sQuery(id+"F11.wireOp",EDGE,"E145")}),-1.0]])]});
            var Q3;
            Q3=makeQuery(id+"F11.imprint","IMPRINT",FACE,{"disambiguationData":[TD([[makeQuery(id+"F11.imprint","IMPRINT",EDGE,{"derivedFrom":sQuery(id+"F11.wireOp",EDGE,"E147")}),-1.0]])]});
            extrude(context, id + "F15", {"entities" : qUnion([Q0, Q1, Q2, Q3]), "operationType" : NewBodyOperationType.REMOVE, "depth" : 27.94 * mm, "hasSecondDirection" : true, "secondDirectionOppositeDirection" : false, "secondDirectionDepth" : 22.86 * mm});
        }
        {
            var Q0;
            Q0=makeQuery(id+"F11.imprint","IMPRINT",FACE,{"disambiguationData":[TD([[makeQuery(id+"F11.imprint","IMPRINT",EDGE,{"derivedFrom":sQuery(id+"F11.wireOp",EDGE,"E145")}),-1.0]])]});
            var Q1;
            Q1=makeQuery(id+"F11.imprint","IMPRINT",FACE,{"disambiguationData":[TD([[makeQuery(id+"F11.imprint","IMPRINT",EDGE,{"derivedFrom":sQuery(id+"F11.wireOp",EDGE,"E145")}),1.0]])]});
            var Q2;
            Q2=makeQuery(id+"F11.imprint","IMPRINT",FACE,{"disambiguationData":[TD([[makeQuery(id+"F11.imprint","IMPRINT",EDGE,{"derivedFrom":sQuery(id+"F11.wireOp",EDGE,"E147")}),1.0]])]});
            var Q3;
            Q3=makeQuery(id+"F11.imprint","IMPRINT",FACE,{"disambiguationData":[TD([[makeQuery(id+"F11.imprint","IMPRINT",EDGE,{"derivedFrom":sQuery(id+"F11.wireOp",EDGE,"E147")}),-1.0]])]});
            extrude(context, id + "F16", {"entities" : qUnion([Q0, Q1, Q2, Q3]), "operationType" : NewBodyOperationType.REMOVE, "oppositeDirection" : true, "depth" : 27.94 * mm, "hasSecondDirection" : true, "secondDirectionOppositeDirection" : true, "secondDirectionDepth" : 22.86 * mm});
        }
        {
            var Q0;
            Q0=makeQuery(id+"F12.imprint","IMPRINT",FACE,{"disambiguationData":[TD([[makeQuery(id+"F12.imprint","IMPRINT",EDGE,{"derivedFrom":sQuery(id+"F12.wireOp",EDGE,"E166")}),1.0]])]});
            var Q1;
            Q1=makeQuery(id+"F12.imprint","IMPRINT",FACE,{"disambiguationData":[TD([[makeQuery(id+"F12.imprint","IMPRINT",EDGE,{"derivedFrom":sQuery(id+"F12.wireOp",EDGE,"E166")}),-1.0]])]});
            extrude(context, id + "F17", {"entities" : qUnion([Q0, Q1]), "operationType" : NewBodyOperationType.REMOVE, "oppositeDirection" : true, "depth" : 27.94 * mm, "hasSecondDirection" : true, "secondDirectionOppositeDirection" : true, "secondDirectionDepth" : 22.86 * mm});
        }
        {
            var Q0;
            {var subQ1=sQuery(id+"F1.wireOp",EDGE,"E48");var subQ2=sQuery(id+"F1.wireOp",EDGE,"E45");var subQ3=sQuery(id+"F1.wireOp",EDGE,"E44");var subQ4=sQuery(id+"F1.wireOp",EDGE,"E42");Q0=makeQuery(id+"F6.boolean.opBoolean","SPLIT",EDGE,{"disambiguationData":[TD([makeQuery(id+"F5.opExtrude","SWEPT_FACE",FACE,{"disambiguationData":[OSD([subQ4])]})])],"derivedFrom":makeQuery(id+"F5.opExtrude","CAP_EDGE",EDGE,{"disambiguationData":[OSD([subQ3,subQ2,subQ1])],"isStart":true})});}
            var Q1;
            Q1=makeQuery(id+"F5.opExtrude","CAP_EDGE",EDGE,{"disambiguationData":[OSD([sQuery(id+"F1.wireOp",EDGE,"E42")])],"isStart":true});
            var Q2;
            Q2=makeQuery(id+"F5.opExtrude","CAP_EDGE",EDGE,{"disambiguationData":[OSD([sQuery(id+"F1.wireOp",EDGE,"E36.MirrorCS")])],"isStart":true});
            var Q3;
            Q3=makeQuery(id+"F5.opExtrude","CAP_EDGE",EDGE,{"disambiguationData":[OSD([sQuery(id+"F1.wireOp",EDGE,"E35.MirrorCS")])],"isStart":true});
            var Q4;
            Q4=makeQuery(id+"F5.opExtrude","CAP_EDGE",EDGE,{"disambiguationData":[OSD([sQuery(id+"F1.wireOp",EDGE,"E28")])],"isStart":true});
            var Q5;
            Q5=makeQuery(id+"F5.opExtrude","CAP_EDGE",EDGE,{"disambiguationData":[OSD([sQuery(id+"F1.wireOp",EDGE,"E34")])],"isStart":true});
            var Q6;
            Q6=makeQuery(id+"F5.opExtrude","CAP_EDGE",EDGE,{"disambiguationData":[OSD([sQuery(id+"F1.wireOp",EDGE,"E53")])],"isStart":true});
            var Q7;
            {var subQ1=sQuery(id+"F1.wireOp",EDGE,"E53");var subQ2=sQuery(id+"F1.wireOp",EDGE,"E52.MirrorCS");var subQ3=sQuery(id+"F1.wireOp",EDGE,"E51.MirrorCS");var subQ4=sQuery(id+"F1.wireOp",EDGE,"E49.MirrorCS");Q7=makeQuery(id+"F6.boolean.opBoolean","SPLIT",EDGE,{"disambiguationData":[TD([makeQuery(id+"F5.opExtrude","SWEPT_FACE",FACE,{"disambiguationData":[OSD([subQ1])]})])],"derivedFrom":makeQuery(id+"F5.opExtrude","CAP_EDGE",EDGE,{"disambiguationData":[OSD([subQ4,subQ3,subQ2])],"isStart":true})});}
            var Q8;
            Q8=makeQuery(id+"F5.opExtrude","CAP_EDGE",EDGE,{"disambiguationData":[OSD([sQuery(id+"F1.wireOp",EDGE,"E57")])],"isStart":true});
            fillet(context, id + "F18", {"entities" : qUnion([Q0, Q1, Q2, Q3, Q4, Q5, Q6, Q7, Q8]), "radius" : 2.54 * mm, "allowEdgeOverflow" : false});
        }
        {
            var Q0;
            Q0=makeQuery(id+"F13.opExtrude","CAP_EDGE",EDGE,{"disambiguationData":[OSD([sQuery(id+"F12.wireOp",EDGE,"E169")])],"isStart":false});
            var Q1;
            {var subQ0=sQuery(id+"F0.wireOp",EDGE,"E0.right");Q1=makeQuery(id+"F16.boolean.opBoolean","INTERSECT",EDGE,{"derivedFrom":[makeQuery(id+"FVeaqIvGeaTVGBi_11.opBoolean","MERGE",FACE,{"derivedFrom":[makeQuery(id+"F5.opExtrude","SWEPT_FACE",FACE,{"disambiguationData":[OSD([subQ0])]}),makeQuery(id+"F8.opExtrude","SWEPT_FACE",FACE,{"disambiguationData":[OSD([subQ0])]})]}),makeQuery(id+"F16.opExtrude","SWEPT_FACE",FACE,{"disambiguationData":[OSD([sQuery(id+"F11.wireOp",EDGE,"E146")])]})]});}
            var Q2;
            {var subQ0=sQuery(id+"F0.wireOp",EDGE,"E0.top");Q2=makeQuery(id+"F17.boolean.opBoolean","INTERSECT",EDGE,{"derivedFrom":[makeQuery(id+"FVeaqIvGeaTVGBi_11.opBoolean","MERGE",FACE,{"derivedFrom":[makeQuery(id+"F5.opExtrude","SWEPT_FACE",FACE,{"disambiguationData":[OSD([subQ0])]}),makeQuery(id+"F8.opExtrude","SWEPT_FACE",FACE,{"disambiguationData":[OSD([subQ0])]})]}),makeQuery(id+"F17.opExtrude","SWEPT_FACE",FACE,{"disambiguationData":[OSD([sQuery(id+"F12.wireOp",EDGE,"E167")])]})]});}
            var Q3;
            {var subQ0=sQuery(id+"F0.wireOp",EDGE,"E0.right");Q3=makeQuery(id+"F16.boolean.opBoolean","INTERSECT",EDGE,{"derivedFrom":[makeQuery(id+"FVeaqIvGeaTVGBi_11.opBoolean","MERGE",FACE,{"derivedFrom":[makeQuery(id+"F5.opExtrude","SWEPT_FACE",FACE,{"disambiguationData":[OSD([subQ0]),TDD([makeQuery(id+"F0.imprint","IMPRINT",EDGE,{"disambiguationData":[TD([[makeQuery(id+"F0.imprint","INTERSECT",VERTEX,{"derivedFrom":[sQuery(id+"F0.wireOp",EDGE,"E0.bottom"),subQ0]}),-1.0]])],"derivedFrom":subQ0})])]}),makeQuery(id+"F5.opExtrude","SWEPT_FACE",FACE,{"disambiguationData":[OSD([subQ0]),TDD([makeQuery(id+"F0.imprint","IMPRINT",EDGE,{"disambiguationData":[TD([[makeQuery(id+"F0.imprint","INTERSECT",VERTEX,{"derivedFrom":[sQuery(id+"F0.wireOp",EDGE,"E0.top"),subQ0]}),1.0]])],"derivedFrom":subQ0})])]}),makeQuery(id+"F8.opExtrude","SWEPT_FACE",FACE,{"disambiguationData":[OSD([subQ0])]})]}),makeQuery(id+"F16.opExtrude","SWEPT_FACE",FACE,{"disambiguationData":[OSD([sQuery(id+"F11.wireOp",EDGE,"E148")])]})]});}
            var Q4;
            Q4=makeQuery(id+"F14.opExtrude","CAP_EDGE",EDGE,{"disambiguationData":[OSD([sQuery(id+"F12.wireOp",EDGE,"E166")])],"isStart":false});
            var Q5;
            Q5=makeQuery(id+"F14.opExtrude","CAP_EDGE",EDGE,{"disambiguationData":[OSD([sQuery(id+"F12.wireOp",EDGE,"E169")])],"isStart":false});
            var Q6;
            {var subQ0=sQuery(id+"F0.wireOp",EDGE,"Muu1YjY4-Iba0-i3kg-3BiW-mJ0jcTlb6XiY");var subQ1=sQuery(id+"F0.wireOp",EDGE,"E0.left");Q6=makeQuery(id+"F15.boolean.opBoolean","INTERSECT",EDGE,{"derivedFrom":[makeQuery(id+"FVeaqIvGeaTVGBi_11.opBoolean","MERGE",FACE,{"derivedFrom":[makeQuery(id+"F5.opExtrude","SWEPT_FACE",FACE,{"disambiguationData":[OSD([subQ1]),TDD([makeQuery(id+"F0.imprint","IMPRINT",EDGE,{"disambiguationData":[TD([[makeQuery(id+"F0.imprint","INTERSECT",VERTEX,{"derivedFrom":[subQ1,sQuery(id+"F0.wireOp",EDGE,"lMXQf7WU-VQvn-eUw7-3v8j-XpuHpQXpMMjl")]}),-1.0]])],"derivedFrom":subQ1})])]}),makeQuery(id+"F5.opExtrude","SWEPT_FACE",FACE,{"disambiguationData":[OSD([subQ1]),TDD([makeQuery(id+"F0.imprint","IMPRINT",EDGE,{"disambiguationData":[TD([[makeQuery(id+"F0.imprint","INTERSECT",VERTEX,{"derivedFrom":[sQuery(id+"F0.wireOp",EDGE,"E0.top"),subQ1]}),1.0]])],"derivedFrom":subQ1})])]}),makeQuery(id+"F8.opExtrude","SWEPT_FACE",FACE,{"disambiguationData":[OSD([subQ1,subQ0])]})]}),makeQuery(id+"F15.opExtrude","SWEPT_FACE",FACE,{"disambiguationData":[OSD([sQuery(id+"F11.wireOp",EDGE,"E146")])]})]});}
            var Q7;
            {var subQ0=sQuery(id+"F0.wireOp",EDGE,"Muu1YjY4-Iba0-i3kg-3BiW-mJ0jcTlb6XiY");var subQ1=sQuery(id+"F0.wireOp",EDGE,"E0.left");Q7=makeQuery(id+"F15.boolean.opBoolean","INTERSECT",EDGE,{"derivedFrom":[makeQuery(id+"FVeaqIvGeaTVGBi_11.opBoolean","MERGE",FACE,{"derivedFrom":[makeQuery(id+"F5.opExtrude","SWEPT_FACE",FACE,{"disambiguationData":[OSD([subQ1]),TDD([makeQuery(id+"F0.imprint","IMPRINT",EDGE,{"disambiguationData":[TD([[makeQuery(id+"F0.imprint","INTERSECT",VERTEX,{"derivedFrom":[subQ1,sQuery(id+"F0.wireOp",EDGE,"lMXQf7WU-VQvn-eUw7-3v8j-XpuHpQXpMMjl")]}),-1.0]])],"derivedFrom":subQ1})])]}),makeQuery(id+"F5.opExtrude","SWEPT_FACE",FACE,{"disambiguationData":[OSD([subQ1]),TDD([makeQuery(id+"F0.imprint","IMPRINT",EDGE,{"disambiguationData":[TD([[makeQuery(id+"F0.imprint","INTERSECT",VERTEX,{"derivedFrom":[sQuery(id+"F0.wireOp",EDGE,"E0.top"),subQ1]}),1.0]])],"derivedFrom":subQ1})])]}),makeQuery(id+"F8.opExtrude","SWEPT_FACE",FACE,{"disambiguationData":[OSD([subQ1,subQ0])]})]}),makeQuery(id+"F15.opExtrude","SWEPT_FACE",FACE,{"disambiguationData":[OSD([sQuery(id+"F11.wireOp",EDGE,"E148")])]})]});}
            var Q8;
            Q8=makeQuery(id+"F6.opExtrude","CAP_EDGE",EDGE,{"disambiguationData":[OSD([sQuery(id+"F2.wireOp",EDGE,"E67.MirrorC")])],"isStart":false});
            var Q9;
            Q9=makeQuery(id+"F6.opExtrude","CAP_EDGE",EDGE,{"disambiguationData":[OSD([sQuery(id+"F2.wireOp",EDGE,"E66.MirrorC")])],"isStart":false});
            var Q10;
            Q10=makeQuery(id+"F6.opExtrude","CAP_EDGE",EDGE,{"disambiguationData":[OSD([sQuery(id+"F2.wireOp",EDGE,"E69.MirrorC")])],"isStart":false});
            var Q11;
            Q11=makeQuery(id+"F6.opExtrude","CAP_EDGE",EDGE,{"disambiguationData":[OSD([sQuery(id+"F2.wireOp",EDGE,"E63")])],"isStart":false});
            var Q12;
            Q12=makeQuery(id+"F9.boolean.opBoolean","COPY",EDGE,{"derivedFrom":makeQuery(id+"F9.opExtrude","CAP_EDGE",EDGE,{"disambiguationData":[OSD([sQuery(id+"F2.wireOp",EDGE,"E68.MirrorC")])],"isStart":false})});
            var Q13;
            Q13=makeQuery(id+"F9.boolean.opBoolean","COPY",EDGE,{"derivedFrom":makeQuery(id+"F9.opExtrude","CAP_EDGE",EDGE,{"disambiguationData":[OSD([sQuery(id+"F2.wireOp",EDGE,"E65.MirrorC")])],"isStart":false})});
            var Q14;
            Q14=makeQuery(id+"F9.boolean.opBoolean","COPY",EDGE,{"derivedFrom":makeQuery(id+"F9.opExtrude","CAP_EDGE",EDGE,{"disambiguationData":[OSD([sQuery(id+"F2.wireOp",EDGE,"E70.MirrorC")])],"isStart":false})});
            var Q15;
            Q15=makeQuery(id+"F9.boolean.opBoolean","COPY",EDGE,{"derivedFrom":makeQuery(id+"F9.opExtrude","CAP_EDGE",EDGE,{"disambiguationData":[OSD([sQuery(id+"F2.wireOp",EDGE,"E64")])],"isStart":false})});
            fillet(context, id + "F19", {"entities" : qUnion([Q0, Q1, Q2, Q3, Q4, Q5, Q6, Q7, Q8, Q9, Q10, Q11, Q12, Q13, Q14, Q15]), "radius" : 0.64 * mm, "tangentPropagation" : true, "allowEdgeOverflow" : false});
        }
    });
